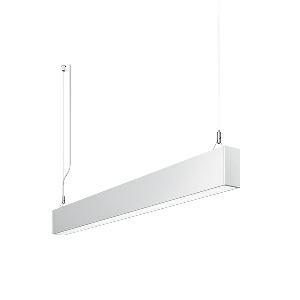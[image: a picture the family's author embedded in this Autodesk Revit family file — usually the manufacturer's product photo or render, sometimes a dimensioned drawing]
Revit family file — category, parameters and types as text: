
# Revit family: idoo_line_-_ilp_4000_840_d_00805675_aa0f
name_source: partatom
category: Lighting Fixtures
units: mm (PartAtom-declared; Revit-internal decimal feet)

## family parameters
Cut with Voids When Loaded = No
Host = Face
Light Source = No
Part Type = Normal
Room Calculation Point = No
Round Connector Dimension = Use Diameter
Shared = No

## types (1)
- IDOO.line - ILP 4000/840/D (1 x LED, 3950 lm, 4000K)
    Apparent Load = 29 VA
    Approval mark = CE
    CIE Flux Codes = 66 91 98 40 100
    Color Rendering = 80-89
    Color Temperature = 4000K
    Control Gear = Electronic ballast
    Default Elevation = 1800 mm
    Description = ILP 4000/840/D|Suspended luminaire|light source: LED Cold white   |standby: approx. 0,15|luminous flux: 3950 lm|light distribution: Direct/indirect|direct ratio: approx. 40 %|color rendering index (CRI): >= 80|chromaticity tolerance:  3 SDCM|System of protection: IP 40|technology: Continuously dimmable|luminaire body|material: Sectional aluminium|colour: White|lamp cover: Acrylic (PMMA), Clear|mains lead: 2.00 m With free stranded wires|Fastening: Steel cable 0.3 - 0.7 m|glare control: Prism aperture|luminance(L65): <= 2700 cd/m|unified glare rating(4H 8H): <=  16|special features: DALI Load 1x, TouchDIM - dimming via standard switch, Flicker-free, Suitable as emergency lighting|
    Frequency = 50 Hz
    Height = 110 mm
    Lamp = 1 x LED
    Lamp Light Flux = 3950 lm
    Lamp count = 1
    Length = 1414 mm
    Luminous efficacy = 136 lm/W
    Manufacturer = Waldmann
    ModVariant = No
    Model = 00805675
    Mounting Place = Ceiling
    Mounting Type = Pendant
    Number of Poles = 1
    OnlyDefault = Yes
    Power Factor = 1
    Product Name = IDOO.line - ILP 4000/840/D
    Product group = Suspended luminaire
    ProductGroupID = 9
    Protection Class = Protection class I
    Protection Degree = IP 40
    RLX_Detail_Level = 1
    RLX_Emergency_Light_Flux = 0 lm
    RLX_Emergency_Type = 0
    RLX_Emergency_Type_DB = No
    RlxData = <blob elided: 19129 chars, md5=f7f3a867>
    Socket = socket
    Standby Power = 0 W
    System Light Flux = 3950 lm
    System Power = 29 W
    Type Comments = Product without accessories
    Type Image = 113291000-00692522.jpg
    URL = http://relux.com
    VarID = ---
    Voltage = 230 V
    Voltage Range = 220-240 V
    Weight = 0.00 kg
    Width = 60 mm  [stored 0.19685 ft]

note: [stored X ft] marks values corroborated as IEEE doubles in the binary element streams (Revit-internal decimal feet)

## geometry (parser evidence)
native form markers: Blend x4, Sweep x12
no freeform markers — native parametric forms only
